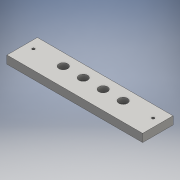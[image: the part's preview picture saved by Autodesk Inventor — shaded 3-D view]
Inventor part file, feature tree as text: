
AUTODESK INVENTOR PART (.ipt)
format: ipt  version: 2016 (Build 200138000, 138)  size: 120,832 bytes
history: native  units: mm
features: sketch x3, hole x2, extrude x1
ambient origin geometry x8: Origin, YZ Plane, XZ Plane, XY Plane, X Axis, Y Axis, Z Axis, Center Point
bodies: Solid1 (feature_tree)
feature tree (6):
  extrude  "Extrusion1"  Depth=170.0mm
  hole  "Hole1"  [1 undecoded]
  hole  "Hole2"  [1 undecoded]
  sketch  "Sketch1"  dims[d0=30.0mm d1=170.0mm]
  sketch  "Sketch2"  dims[d2=85.0mm d3=15.0mm]
  sketch  "Sketch3"  dims[d4=10.0mm d5=0.0mm d9=6.6mm d10=6.0mm d11=11.0mm d12=7.0mm d13=90.0deg d14=8.0mm d15=20.594885mm d16=150.0mm d17=75.0mm d19=3.242mm d20=8.0mm d21=19.05mm d22=4.775mm d23=90.0deg d24=11.8mm d25=20.594885mm d30=25.0mm d31=25.0mm d32=25.0mm d33=12.5mm d34=8.1mm d35=170.0mm]
note: 2 required parameter values undecoded (feature->parameter linkage not recoverable at this tier; creation-order binding heuristic only, values carry confidence <= 0.55)
